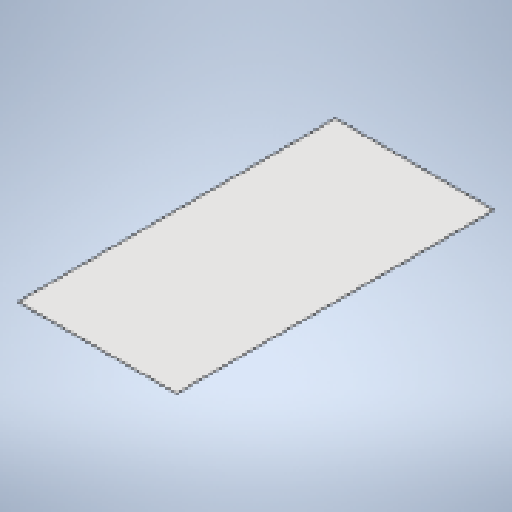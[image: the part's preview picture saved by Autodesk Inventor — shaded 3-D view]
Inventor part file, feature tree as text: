
AUTODESK INVENTOR PART (.ipt)
format: ipt  version: 2025.3 (Build 293356000, 356)  size: 122,880 bytes
history: native  units: mm
features: sheet_metal_op x1, sketch x1, other x1
ambient origin geometry x8: Origin, YZ Plane, XZ Plane, XY Plane, X Axis, Y Axis, Z Axis, Center Point
bodies: Solid1 (feature_tree)
feature tree (3):
  sheet_metal_op  "Face1"
  sketch  "Sketch1"  dims[d0=1250.0mm d1=2100.0mm d2=3.0mm d22=35.0mm d23=35.0mm]
  other  "Plate1"
